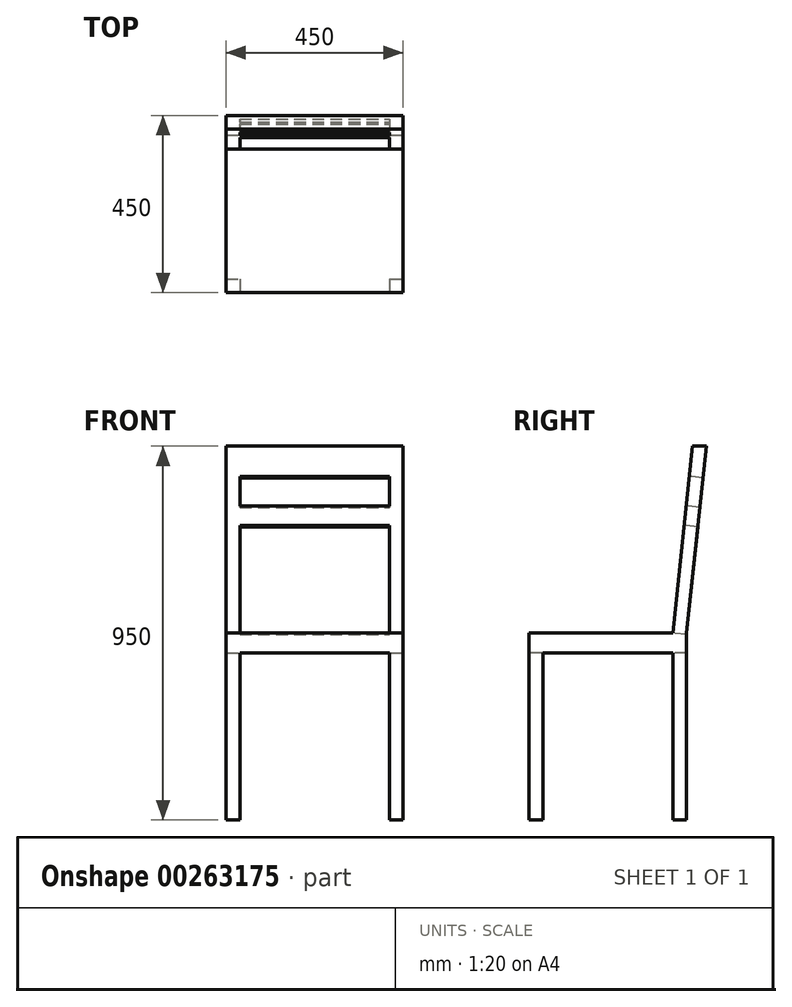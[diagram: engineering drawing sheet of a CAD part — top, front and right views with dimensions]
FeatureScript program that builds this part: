
annotation { "Feature Type Name" : "Feature", "Feature Type Description" : "" }
export const myFeature = defineFeature(function(context is Context, id is Id, definition is map)
    precondition{}
    {
        {
            var Q0;
            Q0=qCreatedBy(makeId("Top.planeOp"),FACE);
            var sketch = newSketch(context, id + "F0", { "sketchPlane" : qUnion([Q0])});
            skLineSegment(sketch, "E0.bottom", {"start": v(225, 225) * mm, "end": v(-225, 225) * mm});
            skLineSegment(sketch, "E0.top", {"start": v(225, -225) * mm, "end": v(-225, -225) * mm});
            skLineSegment(sketch, "E0.left", {"start": v(225, 225) * mm, "end": v(225, -225) * mm});
            skLineSegment(sketch, "E0.right", {"start": v(-225, 225) * mm, "end": v(-225, -225) * mm});
            skPoint(sketch, "E0.middle", {"position": v(0, 0) * mm});
            skSolve(sketch);
        }
        {
            var Q0;
            Q0=qSketchRegion(id+"F0",true);
            extrude(context, id + "F1", {"entities" : qUnion([Q0]), "depth" : 950 * mm});
        }
        {
            var Q0;
            Q0=makeQuery(id+"F1.opExtrude","SWEPT_FACE",FACE,{"disambiguationData":[OSD([sQuery(id+"F0.wireOp",EDGE,"E0.left")])]});
            var sketch = newSketch(context, id + "F2", { "sketchPlane" : qUnion([Q0])});
            skLineSegment(sketch, "E1.bottom", {"start": v(-225, 475) * mm, "end": v(225, 475) * mm});
            skLineSegment(sketch, "E1.top", {"start": v(-225, 425) * mm, "end": v(225, 425) * mm});
            skLineSegment(sketch, "E1.left", {"start": v(-225, 475) * mm, "end": v(-225, 425) * mm});
            skLineSegment(sketch, "E1.right", {"start": v(225, 475) * mm, "end": v(225, 425) * mm});
            skLineSegment(sketch, "E2", {"start": v(225, 950) * mm, "end": v(175, 475) * mm});
            skLineSegment(sketch, "E3", {"start": v(190, 950) * mm, "end": v(140, 475) * mm});
            skLineSegment(sketch, "E4", {"start": v(175, 475) * mm, "end": v(175, 0) * mm});
            skLineSegment(sketch, "E5", {"start": v(140, 475) * mm, "end": v(140, 0) * mm});
            skLineSegment(sketch, "E6", {"start": v(-190, 0) * mm, "end": v(-190, 425) * mm});
            skSolve(sketch);
        }
        {
            var Q0;
            {var subQ4=sQuery(id+"F2.wireOp",EDGE,"E3");Q0=makeQuery(id+"F2.imprint","IMPRINT",FACE,{"disambiguationData":[TD([[makeQuery(id+"F2.imprint","IMPRINT",EDGE,{"derivedFrom":subQ4}),-1.0]])]});}
            var Q1;
            {var subQ4=sQuery(id+"F2.wireOp",EDGE,"E2");Q1=makeQuery(id+"F2.imprint","IMPRINT",FACE,{"disambiguationData":[TD([[makeQuery(id+"F2.imprint","IMPRINT",EDGE,{"derivedFrom":subQ4}),1.0]])]});}
            var Q2;
            {var subQ0=sQuery(id+"F2.wireOp",EDGE,"E1.right");Q2=makeQuery(id+"F2.imprint","IMPRINT",FACE,{"disambiguationData":[TD([[makeQuery(id+"F2.imprint","IMPRINT",EDGE,{"derivedFrom":subQ0}),-1.0]])]});}
            var Q3;
            {var subQ1=sQuery(id+"F0.wireOp",EDGE,"E0.left");var subQ4=sQuery(id+"F2.wireOp",EDGE,"E4");var subQ6=makeQuery(id+"F1.opExtrude","CAP_EDGE",EDGE,{"disambiguationData":[OSD([subQ1])],"isStart":true});var subQ7=makeQuery(id+"F2.imprint","INTERSECT",VERTEX,{"derivedFrom":[subQ6,subQ4]});Q3=makeQuery(id+"F2.imprint","IMPRINT",FACE,{"disambiguationData":[TD([[makeQuery(id+"F2.imprint","IMPRINT",EDGE,{"disambiguationData":[TD([[subQ7,1.0]])],"derivedFrom":subQ4}),1.0]])]});}
            var Q4;
            {var subQ0=sQuery(id+"F2.wireOp",EDGE,"E6");Q4=makeQuery(id+"F2.imprint","IMPRINT",FACE,{"disambiguationData":[TD([[makeQuery(id+"F2.imprint","IMPRINT",EDGE,{"derivedFrom":subQ0}),-1.0]])]});}
            extrude(context, id + "F3", {"entities" : qUnion([Q0, Q1, Q2, Q3, Q4]), "operationType" : NewBodyOperationType.REMOVE, "endBound" : BoundingType.THROUGH_ALL, "oppositeDirection" : true, "depth" : 25 * mm});
        }
        {
            var Q0;
            Q0=makeQuery(id+"F1.opExtrude","SWEPT_FACE",FACE,{"disambiguationData":[OSD([sQuery(id+"F0.wireOp",EDGE,"E0.top")])]});
            var sketch = newSketch(context, id + "F4", { "sketchPlane" : qUnion([Q0])});
            skLineSegment(sketch, "E7.bottom", {"start": v(-190, 0) * mm, "end": v(190, 0) * mm});
            skLineSegment(sketch, "E7.top", {"start": v(-190, 425) * mm, "end": v(190, 425) * mm});
            skLineSegment(sketch, "E7.left", {"start": v(-190, 0) * mm, "end": v(-190, 425) * mm});
            skLineSegment(sketch, "E7.right", {"start": v(190, 0) * mm, "end": v(190, 425) * mm});
            skSolve(sketch);
        }
        {
            var Q0;
            Q0=makeQuery(id+"F4.imprint","IMPRINT",FACE,{"disambiguationData":[TD([[makeQuery(id+"F4.imprint","IMPRINT",EDGE,{"derivedFrom":sQuery(id+"F4.wireOp",EDGE,"E7.bottom")}),-1.0]])]});
            extrude(context, id + "F5", {"entities" : qUnion([Q0]), "operationType" : NewBodyOperationType.REMOVE, "endBound" : BoundingType.THROUGH_ALL, "oppositeDirection" : true, "depth" : 25 * mm});
        }
        {
            var Q0;
            Q0=makeQuery(id+"F3.boolean.opBoolean","COPY",FACE,{"derivedFrom":makeQuery(id+"F3.opExtrude","SWEPT_FACE",FACE,{"disambiguationData":[OSD([sQuery(id+"F2.wireOp",EDGE,"E3")])]})});
            var sketch = newSketch(context, id + "F6", { "sketchPlane" : qUnion([Q0])});
            skLineSegment(sketch, "E8", {"start": v(-190, 487.05) * mm, "end": v(-190, 887.05) * mm});
            skLineSegment(sketch, "E9", {"start": v(-190, 887.05) * mm, "end": v(190, 887.05) * mm});
            skLineSegment(sketch, "E10", {"start": v(190, 887.05) * mm, "end": v(190, 487.05) * mm});
            skLineSegment(sketch, "E11.bottom", {"start": v(-190, 762.05) * mm, "end": v(190, 762.05) * mm});
            skLineSegment(sketch, "E11.top", {"start": v(-190, 812.05) * mm, "end": v(190, 812.05) * mm});
            skLineSegment(sketch, "E11.left", {"start": v(-190, 762.05) * mm, "end": v(-190, 812.05) * mm});
            skLineSegment(sketch, "E11.right", {"start": v(190, 762.05) * mm, "end": v(190, 812.05) * mm});
            skSolve(sketch);
        }
        {
            var Q0;
            {var subQ0=sQuery(id+"F6.wireOp",EDGE,"E9");Q0=makeQuery(id+"F6.imprint","IMPRINT",FACE,{"disambiguationData":[TD([[makeQuery(id+"F6.imprint","IMPRINT",EDGE,{"derivedFrom":subQ0}),-1.0]])]});}
            var Q1;
            {var subQ3=sQuery(id+"F6.wireOp",EDGE,"E11.bottom");Q1=makeQuery(id+"F6.imprint","IMPRINT",FACE,{"disambiguationData":[TD([[makeQuery(id+"F6.imprint","IMPRINT",EDGE,{"derivedFrom":subQ3}),-1.0]])]});}
            extrude(context, id + "F7", {"entities" : qUnion([Q0, Q1]), "operationType" : NewBodyOperationType.REMOVE, "endBound" : BoundingType.THROUGH_ALL, "oppositeDirection" : true, "depth" : 25 * mm});
        }
    });
